# Revit family: Storage-Teknion-LWBTH_Byward_High_Tower-R2022
name_source: partatom
category: Furniture
units: mm (PartAtom-declared; Revit-internal decimal feet)

## family parameters
Always vertical = Yes
Cut with Voids When Loaded = No
OmniClass Number = 23.40.20.00
OmniClass Title = General Furniture and Specialties
Render Appearance Source = Family Geometry
Room Calculation Point = No
Shared = Yes
Work Plane-Based = No

## types (4) — shared parameters
Assembly Code = E2020200
Manufacturer = Teknion
Manufacturer Fax = 416.661.4586
OJ = No
Part Number = LWBTH
Product Documentation Link = https://www.teknion.com
Product Line = Byward
Product Page URL = https://www.teknion.com
Series = Byward
Sustainability Data = https://www.teknion.com
URL = www.teknion.com
Unit Weight URL = http://www.teknion.com
Warranty = http://www.teknion.com
zero-valued in all types: Default Elevation

## per-type parameters (varying)
| type | CC | Description | JO | Left Door Double Handle | Left Door Single Handle | Left Door Visibility | Model | OO | Right Door Double Handle | Right Door Single Handle | Right Door Visibility |
| All Closed | Yes | Byward High Tower, All Closed | No | No | Yes | Yes | LWBTHCC60_____ | No | Yes | Yes | Yes |
| Left Coat, Right Open | No | Byward High Tower, Left Coat, Right Open | Yes | Yes | Yes | Yes | LWBTHJO60_____ | No | No | No | No |
| All Open | No | Byward High Tower, All Open | No | No | No | No | LWBTHOO60_____ | Yes | No | No | No |
| Left Closed, Right Coat | Yes | Byward High Tower, Left Closed Right Coat | No | No | Yes | Yes | LWBTHCJ60_____ | No | Yes | Yes | Yes |

## geometry (parser evidence)
native form markers: Sweep x10
no freeform markers — native parametric forms only
